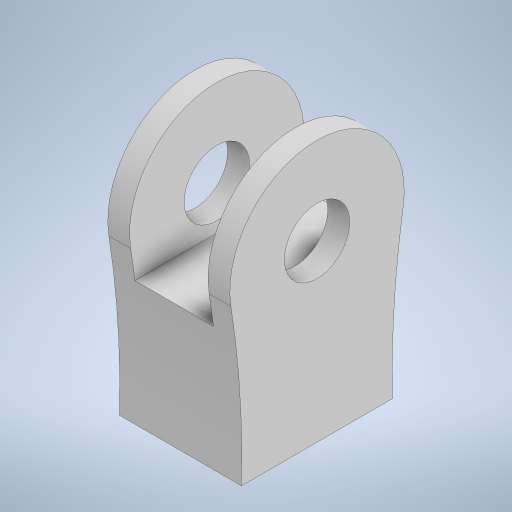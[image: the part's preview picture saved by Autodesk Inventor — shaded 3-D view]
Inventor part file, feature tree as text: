
AUTODESK INVENTOR PART (.ipt)
format: ipt  version: 2023.2 (Build 272271030, 271C)  size: 269,312 bytes
history: native  units: mm
features: extrude x4, sketch x3, projected_geometry x2
ambient origin geometry x8: Origin, YZ Plane, XZ Plane, XY Plane, X Axis, Y Axis, Z Axis, Center Point
bodies: Solid1 (feature_tree)
feature tree (9):
  extrude  "Extrusion1"  Depth=40.0mm
  extrude  "Extrusion3"  Depth=34.667mm
  sketch  "Sketch4"  dims[d10=10.0mm d11=30.0mm d12=28.0mm d13=0.0mm d19=18.0mm d21=10.0mm d22=0.0mm d23=0.0mm d24=8.6mm d25=5.5mm d26=3.3mm d27=0.0mm d28=0.0mm d29=0.0mm]
  extrude  "Extrusion4"  Depth=30.0mm
  extrude  "Extrusion5"  Depth=28.0mm TaperAngle=0.0deg
  sketch  "Sketch1"  dims[d6=15.0mm d7=40.0mm]
  sketch  "Sketch3"  dims[d8=400.0mm d9=34.667mm]
  projected_geometry  "Projected Loop3"
  projected_geometry  "Projected Loop4"
